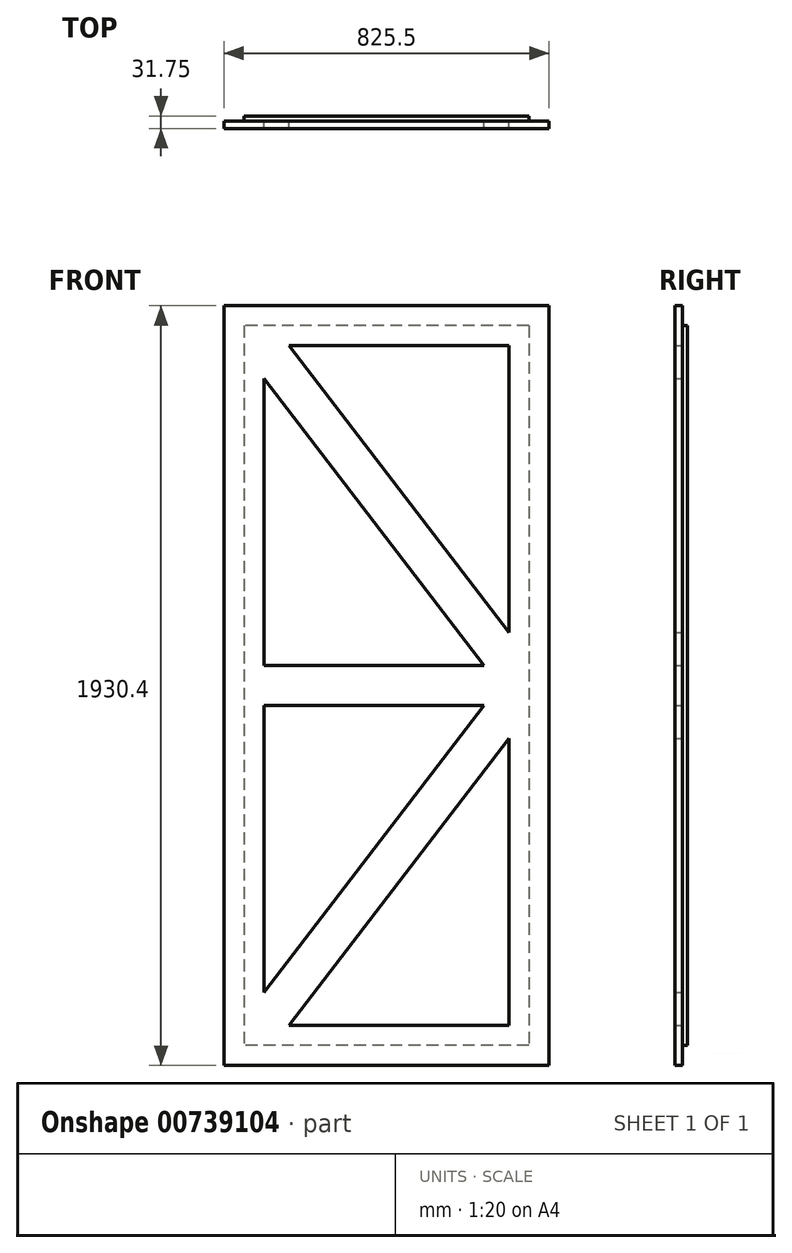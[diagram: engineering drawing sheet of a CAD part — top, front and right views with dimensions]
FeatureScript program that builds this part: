
annotation { "Feature Type Name" : "Feature", "Feature Type Description" : "" }
export const myFeature = defineFeature(function(context is Context, id is Id, definition is map)
    precondition{}
    {
        {
            var Q0;
            Q0=qCreatedBy(makeId("Front.planeOp"),FACE);
            var sketch = newSketch(context, id + "F0", { "sketchPlane" : qUnion([Q0])});
            skLineSegment(sketch, "E0.bottom", {"start": v(0, 0) * mm, "end": v(825.5, 0) * mm});
            skLineSegment(sketch, "E0.top", {"start": v(0, 1930.4) * mm, "end": v(825.5, 1930.4) * mm});
            skLineSegment(sketch, "E0.left", {"start": v(0, 0) * mm, "end": v(0, 1930.4) * mm});
            skLineSegment(sketch, "E0.right", {"start": v(825.5, 0) * mm, "end": v(825.5, 1930.4) * mm});
            skLineSegment(sketch, "E1.0", {"start": v(101.6, 101.6) * mm, "end": v(101.6, 1828.8) * mm});
            skLineSegment(sketch, "E1.1", {"start": v(101.6, 101.6) * mm, "end": v(723.9, 101.6) * mm});
            skLineSegment(sketch, "E1.2", {"start": v(723.9, 101.6) * mm, "end": v(723.9, 1828.8) * mm});
            skLineSegment(sketch, "E1.3", {"start": v(101.6, 1828.8) * mm, "end": v(723.9, 1828.8) * mm});
            skLineSegment(sketch, "E2", {"start": v(101.6, 965.2) * mm, "end": v(723.9, 965.2) * mm});
            skLineSegment(sketch, "E3.0", {"start": v(101.6, 1016) * mm, "end": v(723.9, 1016) * mm});
            skLineSegment(sketch, "E4.0", {"start": v(101.6, 914.4) * mm, "end": v(723.9, 914.4) * mm});
            skLineSegment(sketch, "E5", {"start": v(101.6, 1828.8) * mm, "end": v(723.9, 1016) * mm});
            skLineSegment(sketch, "E6", {"start": v(101.6, 101.6) * mm, "end": v(723.9, 914.4) * mm});
            skLineSegment(sketch, "E7.0", {"start": v(61.26, 1797.92) * mm, "end": v(683.56, 985.12) * mm});
            skLineSegment(sketch, "E8.0", {"start": v(141.94, 1859.68) * mm, "end": v(764.24, 1046.88) * mm});
            skLineSegment(sketch, "E9.0", {"start": v(141.94, 70.72) * mm, "end": v(764.24, 883.52) * mm});
            skLineSegment(sketch, "E10.0", {"start": v(61.26, 132.48) * mm, "end": v(683.56, 945.28) * mm});
            skSolve(sketch);
        }
        {
            var Q0;
            Q0=makeQuery(id+"F0.imprint","IMPRINT",FACE,{"disambiguationData":[TD([[makeQuery(id+"F0.imprint","IMPRINT",EDGE,{"derivedFrom":sQuery(id+"F0.wireOp",EDGE,"E0.bottom")}),1.0]])]});
            var Q1;
            {var subQ0=sQuery(id+"F0.wireOp",EDGE,"E5");Q1=makeQuery(id+"F0.imprint","IMPRINT",FACE,{"disambiguationData":[TD([[makeQuery(id+"F0.imprint","IMPRINT",EDGE,{"derivedFrom":subQ0}),-1.0]])]});}
            var Q2;
            {var subQ0=sQuery(id+"F0.wireOp",EDGE,"E5");Q2=makeQuery(id+"F0.imprint","IMPRINT",FACE,{"disambiguationData":[TD([[makeQuery(id+"F0.imprint","IMPRINT",EDGE,{"derivedFrom":subQ0}),1.0]])]});}
            var Q3;
            {var subQ4=sQuery(id+"F0.wireOp",EDGE,"E2");Q3=makeQuery(id+"F0.imprint","IMPRINT",FACE,{"disambiguationData":[TD([[makeQuery(id+"F0.imprint","IMPRINT",EDGE,{"derivedFrom":subQ4}),1.0]])]});}
            var Q4;
            {var subQ4=sQuery(id+"F0.wireOp",EDGE,"E2");Q4=makeQuery(id+"F0.imprint","IMPRINT",FACE,{"disambiguationData":[TD([[makeQuery(id+"F0.imprint","IMPRINT",EDGE,{"derivedFrom":subQ4}),-1.0]])]});}
            var Q5;
            {var subQ0=sQuery(id+"F0.wireOp",EDGE,"E6");Q5=makeQuery(id+"F0.imprint","IMPRINT",FACE,{"disambiguationData":[TD([[makeQuery(id+"F0.imprint","IMPRINT",EDGE,{"derivedFrom":subQ0}),1.0]])]});}
            var Q6;
            {var subQ0=sQuery(id+"F0.wireOp",EDGE,"E6");Q6=makeQuery(id+"F0.imprint","IMPRINT",FACE,{"disambiguationData":[TD([[makeQuery(id+"F0.imprint","IMPRINT",EDGE,{"derivedFrom":subQ0}),-1.0]])]});}
            extrude(context, id + "F1", {"entities" : qUnion([Q0, Q1, Q2, Q3, Q4, Q5, Q6]), "depth" : 19.05 * mm, "offsetDistance" : 25.4 * mm});
        }
        {
            var Q0;
            Q0=makeQuery(id+"F1.opExtrude","CAP_FACE",FACE,{"disambiguationData":[OSD([sQuery(id+"F0.wireOp",EDGE,"E0.bottom"),sQuery(id+"F0.wireOp",EDGE,"E0.top"),sQuery(id+"F0.wireOp",EDGE,"E0.left"),sQuery(id+"F0.wireOp",EDGE,"E0.right"),sQuery(id+"F0.wireOp",EDGE,"E1.0"),sQuery(id+"F0.wireOp",EDGE,"E1.1"),sQuery(id+"F0.wireOp",EDGE,"E1.2"),sQuery(id+"F0.wireOp",EDGE,"E1.3"),sQuery(id+"F0.wireOp",EDGE,"E3.0"),sQuery(id+"F0.wireOp",EDGE,"E4.0"),sQuery(id+"F0.wireOp",EDGE,"E7.0"),sQuery(id+"F0.wireOp",EDGE,"E8.0"),sQuery(id+"F0.wireOp",EDGE,"E9.0"),sQuery(id+"F0.wireOp",EDGE,"E10.0")])],"isStart":true});
            var sketch = newSketch(context, id + "F2", { "sketchPlane" : qUnion([Q0])});
            skLineSegment(sketch, "E11.bottom", {"start": v(-774.7, 1879.6) * mm, "end": v(-50.8, 1879.6) * mm});
            skLineSegment(sketch, "E11.top", {"start": v(-774.7, 50.8) * mm, "end": v(-50.8, 50.8) * mm});
            skLineSegment(sketch, "E11.left", {"start": v(-774.7, 1879.6) * mm, "end": v(-774.7, 50.8) * mm});
            skLineSegment(sketch, "E11.right", {"start": v(-50.8, 1879.6) * mm, "end": v(-50.8, 50.8) * mm});
            skSolve(sketch);
        }
        {
            var Q0;
            Q0 = qSketchRegion(id + "F2", true);
            extrude(context, id + "F3", {"entities" : qUnion([Q0]), "operationType" : NewBodyOperationType.ADD, "depth" : 12.7 * mm, "offsetDistance" : 25.4 * mm});
        }
    });
